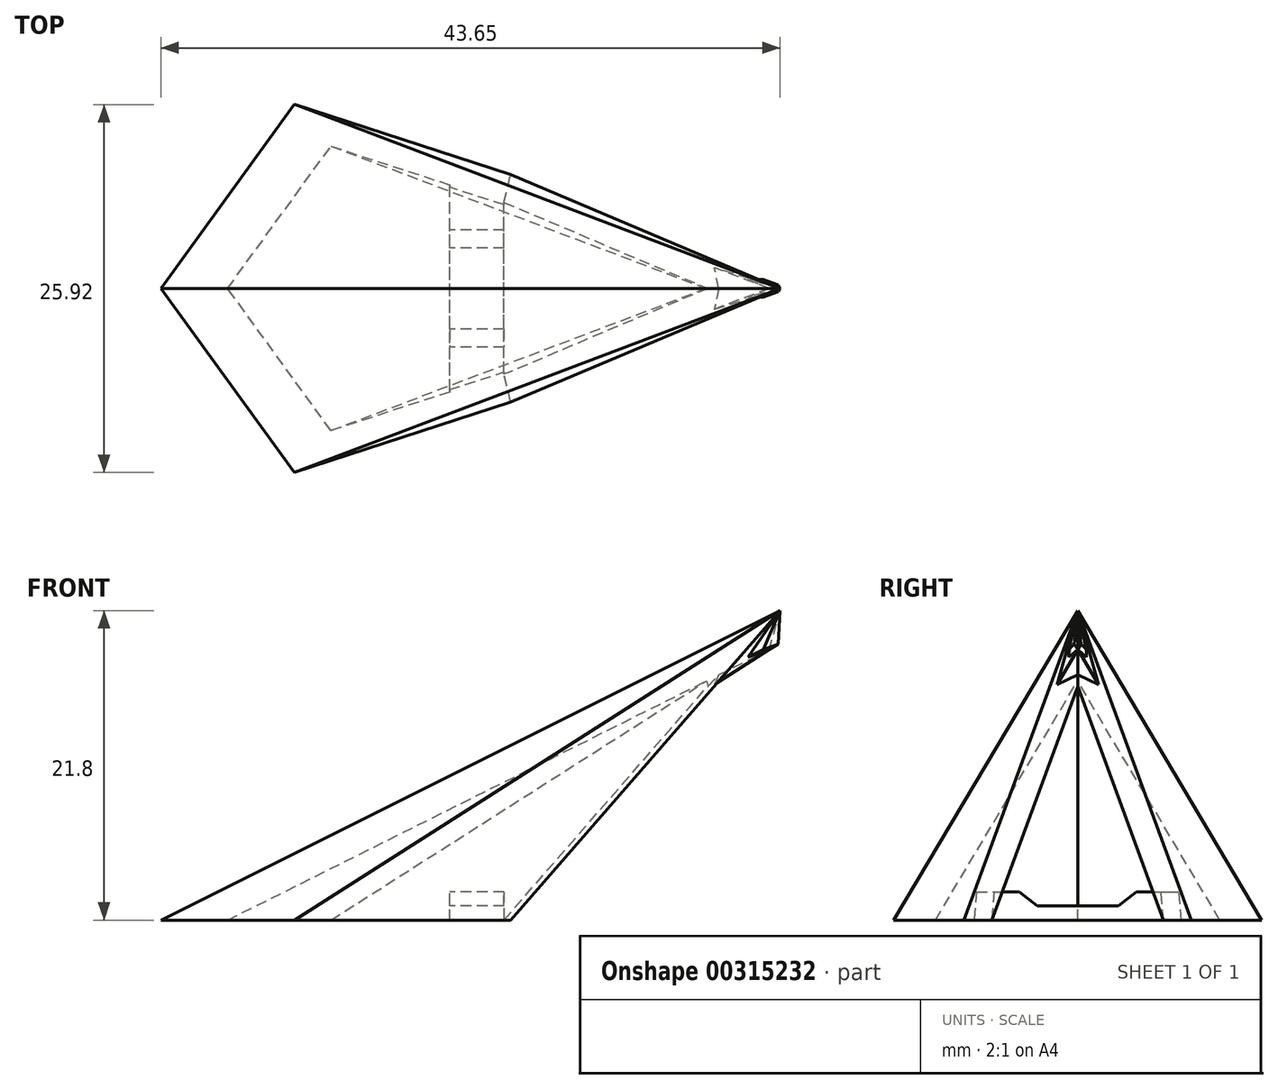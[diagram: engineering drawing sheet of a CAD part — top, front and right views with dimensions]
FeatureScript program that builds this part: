
annotation { "Feature Type Name" : "Feature", "Feature Type Description" : "" }
export const myFeature = defineFeature(function(context is Context, id is Id, definition is map)
    precondition{}
    {
        {
            var Q0;
            Q0=qCreatedBy(makeId("Top.planeOp"),FACE);
            var sketch = newSketch(context, id + "F0", { "sketchPlane" : qUnion([Q0])});
            skCircle(sketch, "E0.cCircle", {"center": v(0, 0) * mm, "radius": 11.03 * mm, "construction": true});
            skLineSegment(sketch, "E0.0", {"start": v(11.03, 8.01) * mm, "end": v(11.03, -8.01) * mm});
            skLineSegment(sketch, "E0.1", {"start": v(11.03, -8.01) * mm, "end": v(-4.21, -12.96) * mm});
            skLineSegment(sketch, "E0.2", {"start": v(-4.21, -12.96) * mm, "end": v(-13.63, 0) * mm});
            skLineSegment(sketch, "E0.3", {"start": v(-13.63, 0) * mm, "end": v(-4.21, 12.96) * mm});
            skLineSegment(sketch, "E0.4", {"start": v(-4.21, 12.96) * mm, "end": v(11.03, 8.01) * mm});
            skPoint(sketch, "E0.0.midPoint", {"position": v(11.03, 0) * mm});
            skSolve(sketch);
        }
        {
            var Q0;
            Q0=qCreatedBy(makeId("Front.planeOp"),FACE);
            var sketch = newSketch(context, id + "F1", { "sketchPlane" : qUnion([Q0])});
            skLineSegment(sketch, "E1", {"start": v(0, 0) * mm, "end": v(30.02, 21.8) * mm});
            skSolve(sketch);
        }
        {
            var Q0;
            Q0=sQuery(id+"F1.wireOp",VERTEX,"E1.end");
            var Q1;
            Q1=sQuery(id+"F0.wireOp",VERTEX,"E0.1.start");
            var Q2;
            Q2=sQuery(id+"F0.wireOp",VERTEX,"E0.2.start");
            cPlane(context, id + "F2", {"entities" : qUnion([Q0, Q1, Q2]), "cplaneType" : CPlaneType.THREE_POINT, "offset" : 25.4 * mm, "oppositeDirection" : true, "width" : 152.4 * mm, "height" : 152.4 * mm});
        }
        {
            var Q0;
            Q0=sQuery(id+"F0.wireOp",VERTEX,"E0.2.start");
            var Q1;
            Q1=sQuery(id+"F0.wireOp",VERTEX,"E0.3.start");
            var Q2;
            Q2=sQuery(id+"F1.wireOp",VERTEX,"E1.end");
            cPlane(context, id + "F3", {"entities" : qUnion([Q0, Q1, Q2]), "cplaneType" : CPlaneType.THREE_POINT, "offset" : 25.4 * mm, "width" : 152.4 * mm, "height" : 152.4 * mm});
        }
        {
            var Q0;
            Q0=sQuery(id+"F1.wireOp",VERTEX,"E1.end");
            var Q1;
            Q1=sQuery(id+"F0.wireOp",VERTEX,"E0.3.start");
            var Q2;
            Q2=sQuery(id+"F0.wireOp",VERTEX,"E0.4.start");
            cPlane(context, id + "F4", {"entities" : qUnion([Q0, Q1, Q2]), "cplaneType" : CPlaneType.THREE_POINT, "offset" : 25.4 * mm, "width" : 152.4 * mm, "height" : 152.4 * mm});
        }
        {
            var Q0;
            Q0=qCreatedBy(id+"F2.planeOp",FACE);
            var sketch = newSketch(context, id + "F5", { "sketchPlane" : qUnion([Q0])});
            skLineSegment(sketch, "E2", {"start": v(28, 21.72) * mm, "end": v(8.03, -0.67) * mm});
            skLineSegment(sketch, "E3", {"start": v(8.03, -0.67) * mm, "end": v(-7.99, -1.1) * mm});
            skLineSegment(sketch, "E4", {"start": v(-7.99, -1.1) * mm, "end": v(28, 21.72) * mm});
            skSolve(sketch);
        }
        {
            var Q0;
            Q0=qCreatedBy(id+"F3.planeOp",FACE);
            var sketch = newSketch(context, id + "F6", { "sketchPlane" : qUnion([Q0])});
            skLineSegment(sketch, "E5", {"start": v(35.88, 7.43) * mm, "end": v(-1.93, -12.19) * mm});
            skLineSegment(sketch, "E6", {"start": v(-1.93, -12.19) * mm, "end": v(-12.34, 0) * mm});
            skLineSegment(sketch, "E7", {"start": v(-12.34, 0) * mm, "end": v(35.88, 7.43) * mm});
            skSolve(sketch);
        }
        {
            var Q0;
            Q0=qCreatedBy(id+"F4.planeOp",FACE);
            var sketch = newSketch(context, id + "F7", { "sketchPlane" : qUnion([Q0])});
            skLineSegment(sketch, "E8", {"start": v(-1.93, 12.19) * mm, "end": v(-12.34, 0) * mm});
            skLineSegment(sketch, "E9", {"start": v(-12.34, 0) * mm, "end": v(35.88, -7.43) * mm});
            skLineSegment(sketch, "E10", {"start": v(35.88, -7.43) * mm, "end": v(-1.93, 12.19) * mm});
            skSolve(sketch);
        }
        {
            var Q0;
            Q0=sQuery(id+"F0.wireOp",VERTEX,"E0.4.end");
            var Q1;
            Q1=sQuery(id+"F5.wireOp",VERTEX,"E4.end");
            var Q2;
            Q2=sQuery(id+"F7.wireOp",VERTEX,"E10.end");
            cPlane(context, id + "F8", {"entities" : qUnion([Q0, Q1, Q2]), "cplaneType" : CPlaneType.THREE_POINT, "offset" : 25.4 * mm, "width" : 152.4 * mm, "height" : 152.4 * mm});
        }
        {
            var Q0;
            Q0=qCreatedBy(id+"F8.planeOp",FACE);
            var sketch = newSketch(context, id + "F9", { "sketchPlane" : qUnion([Q0])});
            skLineSegment(sketch, "E11", {"start": v(-28, 21.72) * mm, "end": v(7.99, -1.1) * mm});
            skLineSegment(sketch, "E12", {"start": v(7.99, -1.1) * mm, "end": v(-8.03, -0.67) * mm});
            skLineSegment(sketch, "E13", {"start": v(-8.03, -0.67) * mm, "end": v(-28, 21.72) * mm});
            skSolve(sketch);
        }
        {
            var Q0;
            Q0=makeQuery(id+"F9.imprint","IMPRINT",FACE,{"disambiguationData":[TD([[makeQuery(id+"F9.imprint","IMPRINT",EDGE,{"derivedFrom":sQuery(id+"F9.wireOp",EDGE,"E11")}),-1.0]])]});
            extrude(context, id + "F10", {"entities" : qUnion([Q0]), "oppositeDirection" : true, "depth" : 2 * mm});
        }
        {
            var Q0;
            Q0=makeQuery(id+"F7.imprint","IMPRINT",FACE,{"disambiguationData":[TD([[makeQuery(id+"F7.imprint","IMPRINT",EDGE,{"derivedFrom":sQuery(id+"F7.wireOp",EDGE,"E8")}),1.0]])]});
            extrude(context, id + "F11", {"entities" : qUnion([Q0]), "operationType" : NewBodyOperationType.ADD, "oppositeDirection" : true, "depth" : 2 * mm});
        }
        {
            var Q0;
            Q0=makeQuery(id+"F6.imprint","IMPRINT",FACE,{"disambiguationData":[TD([[makeQuery(id+"F6.imprint","IMPRINT",EDGE,{"derivedFrom":sQuery(id+"F6.wireOp",EDGE,"E5")}),-1.0]])]});
            extrude(context, id + "F12", {"entities" : qUnion([Q0]), "operationType" : NewBodyOperationType.ADD, "oppositeDirection" : true, "depth" : 2 * mm});
        }
        {
            var Q0;
            Q0=makeQuery(id+"F5.imprint","IMPRINT",FACE,{"disambiguationData":[TD([[makeQuery(id+"F5.imprint","IMPRINT",EDGE,{"derivedFrom":sQuery(id+"F5.wireOp",EDGE,"E2")}),-1.0]])]});
            extrude(context, id + "F13", {"entities" : qUnion([Q0]), "operationType" : NewBodyOperationType.ADD, "oppositeDirection" : true, "depth" : 2 * mm});
        }
        {
            var Q0;
            Q0=makeQuery(id+"F13.opExtrude","CAP_FACE",FACE,{"disambiguationData":[OSD([sQuery(id+"F5.wireOp",EDGE,"E2"),sQuery(id+"F5.wireOp",EDGE,"E3"),sQuery(id+"F5.wireOp",EDGE,"E4")])],"isStart":true});
            var sketch = newSketch(context, id + "F14", { "sketchPlane" : qUnion([Q0])});
            skLineSegment(sketch, "E14.bottom", {"start": v(21.55, 22.32) * mm, "end": v(30.03, 22.32) * mm});
            skLineSegment(sketch, "E14.top", {"start": v(21.55, 16.8) * mm, "end": v(30.03, 16.8) * mm});
            skLineSegment(sketch, "E14.left", {"start": v(21.55, 22.32) * mm, "end": v(21.55, 16.8) * mm});
            skLineSegment(sketch, "E14.right", {"start": v(30.03, 22.32) * mm, "end": v(30.03, 16.8) * mm});
            skSolve(sketch);
        }
        {
            var Q0;
            Q0 = qSketchRegion(id + "F14", true);
            extrude(context, id + "F15", {"entities" : qUnion([Q0]), "operationType" : NewBodyOperationType.REMOVE, "depth" : 25.4 * mm});
        }
        {
            var Q0;
            Q0=makeQuery(id+"F11.opExtrude","CAP_FACE",FACE,{"disambiguationData":[OSD([sQuery(id+"F7.wireOp",EDGE,"E8"),sQuery(id+"F7.wireOp",EDGE,"E9"),sQuery(id+"F7.wireOp",EDGE,"E10")])],"isStart":true});
            var sketch = newSketch(context, id + "F16", { "sketchPlane" : qUnion([Q0])});
            skLineSegment(sketch, "E15.bottom", {"start": v(43.57, -4.34) * mm, "end": v(21.34, -4.34) * mm});
            skLineSegment(sketch, "E15.top", {"start": v(43.57, -8.99) * mm, "end": v(21.34, -8.99) * mm});
            skLineSegment(sketch, "E15.left", {"start": v(43.57, -4.34) * mm, "end": v(43.57, -8.99) * mm});
            skLineSegment(sketch, "E15.right", {"start": v(21.34, -4.34) * mm, "end": v(21.34, -8.99) * mm});
            skSolve(sketch);
        }
        {
            var Q0;
            Q0 = qSketchRegion(id + "F16", true);
            extrude(context, id + "F17", {"entities" : qUnion([Q0]), "operationType" : NewBodyOperationType.REMOVE, "depth" : 25.4 * mm});
        }
        {
            var Q0;
            Q0=makeQuery(id+"F12.opExtrude","CAP_FACE",FACE,{"disambiguationData":[OSD([sQuery(id+"F6.wireOp",EDGE,"E5"),sQuery(id+"F6.wireOp",EDGE,"E6"),sQuery(id+"F6.wireOp",EDGE,"E7")])],"isStart":true});
            var sketch = newSketch(context, id + "F18", { "sketchPlane" : qUnion([Q0])});
            skLineSegment(sketch, "E16.bottom", {"start": v(31.54, 2.1) * mm, "end": v(39.49, 2.1) * mm});
            skLineSegment(sketch, "E16.top", {"start": v(31.54, 9.38) * mm, "end": v(39.49, 9.38) * mm});
            skLineSegment(sketch, "E16.left", {"start": v(31.54, 2.1) * mm, "end": v(31.54, 9.38) * mm});
            skLineSegment(sketch, "E16.right", {"start": v(39.49, 2.1) * mm, "end": v(39.49, 9.38) * mm});
            skSolve(sketch);
        }
        {
            var Q0;
            Q0 = qSketchRegion(id + "F18", true);
            extrude(context, id + "F19", {"entities" : qUnion([Q0]), "operationType" : NewBodyOperationType.REMOVE, "depth" : 25.4 * mm});
        }
        {
            var Q0;
            Q0=makeQuery(id+"F10.opExtrude","CAP_FACE",FACE,{"disambiguationData":[OSD([sQuery(id+"F9.wireOp",EDGE,"E11"),sQuery(id+"F9.wireOp",EDGE,"E12"),sQuery(id+"F9.wireOp",EDGE,"E13")])],"isStart":true});
            var sketch = newSketch(context, id + "F20", { "sketchPlane" : qUnion([Q0])});
            skLineSegment(sketch, "E17.bottom", {"start": v(-23.79, 12.88) * mm, "end": v(-29.7, 12.88) * mm});
            skLineSegment(sketch, "E17.top", {"start": v(-23.79, 24.27) * mm, "end": v(-29.7, 24.27) * mm});
            skLineSegment(sketch, "E17.left", {"start": v(-23.79, 12.88) * mm, "end": v(-23.79, 24.27) * mm});
            skLineSegment(sketch, "E17.right", {"start": v(-29.7, 12.88) * mm, "end": v(-29.7, 24.27) * mm});
            skSolve(sketch);
        }
        {
            var Q0;
            Q0 = qSketchRegion(id + "F20", true);
            extrude(context, id + "F21", {"entities" : qUnion([Q0]), "operationType" : NewBodyOperationType.REMOVE, "depth" : 25.4 * mm});
        }
        {
            var Q0;
            Q0 = qSketchRegion(id + "F0", true);
            extrude(context, id + "F22", {"entities" : qUnion([Q0]), "operationType" : NewBodyOperationType.REMOVE, "oppositeDirection" : true, "depth" : 25.4 * mm});
        }
        {
            var Q0;
            Q0=makeQuery(id+"F22.boolean.opBoolean","COPY",FACE,{"derivedFrom":makeQuery(id+"F22.opExtrude","CAP_FACE",FACE,{"disambiguationData":[OSD([sQuery(id+"F0.wireOp",EDGE,"E0.0"),sQuery(id+"F0.wireOp",EDGE,"E0.1"),sQuery(id+"F0.wireOp",EDGE,"E0.2"),sQuery(id+"F0.wireOp",EDGE,"E0.3"),sQuery(id+"F0.wireOp",EDGE,"E0.4")])],"isStart":true})});
            var sketch = newSketch(context, id + "F23", { "sketchPlane" : qUnion([Q0])});
            skLineSegment(sketch, "E18", {"start": v(-8.92, 6.48) * mm, "end": v(10.55, -6.06) * mm});
            skLineSegment(sketch, "E19", {"start": v(10.55, 6.06) * mm, "end": v(-8.92, -6.48) * mm});
            skLineSegment(sketch, "E20", {"start": v(10.55, 6.06) * mm, "end": v(10.55, -6.06) * mm});
            skLineSegment(sketch, "E21", {"start": v(6.73, 7.3) * mm, "end": v(6.73, -7.3) * mm});
            skSolve(sketch);
        }
        {
            var Q0;
            {var subQ0=sQuery(id+"F23.wireOp",EDGE,"E20");Q0=makeQuery(id+"F23.imprint","IMPRINT",FACE,{"disambiguationData":[TD([[makeQuery(id+"F23.imprint","IMPRINT",EDGE,{"derivedFrom":subQ0}),-1.0]])]});}
            var Q1;
            {var subQ0=sQuery(id+"F23.wireOp",EDGE,"E18");var subQ14=sQuery(id+"F23.wireOp",EDGE,"E21");var subQ15=makeQuery(id+"F23.imprint","INTERSECT",VERTEX,{"derivedFrom":[subQ0,subQ14]});Q1=makeQuery(id+"F23.imprint","IMPRINT",FACE,{"disambiguationData":[TD([[makeQuery(id+"F23.imprint","IMPRINT",EDGE,{"disambiguationData":[TD([[subQ15,-1.0]])],"derivedFrom":subQ14}),1.0]])]});}
            var Q2;
            {var subQ0=sQuery(id+"F23.wireOp",EDGE,"E19");var subQ23=sQuery(id+"F23.wireOp",EDGE,"E21");var subQ24=makeQuery(id+"F23.imprint","INTERSECT",VERTEX,{"derivedFrom":[subQ0,subQ23]});Q2=makeQuery(id+"F23.imprint","IMPRINT",FACE,{"disambiguationData":[TD([[makeQuery(id+"F23.imprint","IMPRINT",EDGE,{"disambiguationData":[TD([[subQ24,1.0]])],"derivedFrom":subQ23}),1.0]])]});}
            extrude(context, id + "F24", {"entities" : qUnion([Q0, Q1, Q2]), "operationType" : NewBodyOperationType.ADD, "oppositeDirection" : true, "depth" : 2 * mm});
        }
        {
            var Q0;
            Q0=makeQuery(id+"F24.opExtrude","SWEPT_FACE",FACE,{"disambiguationData":[OSD([sQuery(id+"F23.wireOp",EDGE,"E21")])]});
            var sketch = newSketch(context, id + "F25", { "sketchPlane" : qUnion([Q0])});
            skLineSegment(sketch, "E22.bottom", {"start": v(2.86, 1) * mm, "end": v(-2.86, 1) * mm});
            skLineSegment(sketch, "E22.top", {"start": v(2.86, 2) * mm, "end": v(-2.86, 2) * mm});
            skLineSegment(sketch, "E22.left", {"start": v(2.86, 1) * mm, "end": v(2.86, 2) * mm});
            skLineSegment(sketch, "E22.right", {"start": v(-2.86, 1) * mm, "end": v(-2.86, 2) * mm});
            skLineSegment(sketch, "E23", {"start": v(0, 1) * mm, "end": v(0, 2) * mm});
            skLineSegment(sketch, "E24", {"start": v(2.86, 1) * mm, "end": v(4.13, 2) * mm});
            skLineSegment(sketch, "E25", {"start": v(-2.86, 1) * mm, "end": v(-4.13, 2) * mm});
            skSolve(sketch);
        }
        {
            var Q0;
            {var subQ0=sQuery(id+"F25.wireOp",EDGE,"E22.left");Q0=makeQuery(id+"F25.imprint","IMPRINT",FACE,{"disambiguationData":[TD([[makeQuery(id+"F25.imprint","IMPRINT",EDGE,{"derivedFrom":subQ0}),-1.0]])]});}
            var Q1;
            {var subQ0=sQuery(id+"F25.wireOp",EDGE,"E22.left");Q1=makeQuery(id+"F25.imprint","IMPRINT",FACE,{"disambiguationData":[TD([[makeQuery(id+"F25.imprint","IMPRINT",EDGE,{"derivedFrom":subQ0}),1.0]])]});}
            var Q2;
            {var subQ0=sQuery(id+"F25.wireOp",EDGE,"E22.right");Q2=makeQuery(id+"F25.imprint","IMPRINT",FACE,{"disambiguationData":[TD([[makeQuery(id+"F25.imprint","IMPRINT",EDGE,{"derivedFrom":subQ0}),-1.0]])]});}
            var Q3;
            {var subQ0=sQuery(id+"F25.wireOp",EDGE,"E22.right");Q3=makeQuery(id+"F25.imprint","IMPRINT",FACE,{"disambiguationData":[TD([[makeQuery(id+"F25.imprint","IMPRINT",EDGE,{"derivedFrom":subQ0}),1.0]])]});}
            extrude(context, id + "F26", {"entities" : qUnion([Q0, Q1, Q2, Q3]), "operationType" : NewBodyOperationType.REMOVE, "oppositeDirection" : true, "depth" : 25.4 * mm});
        }
    });
